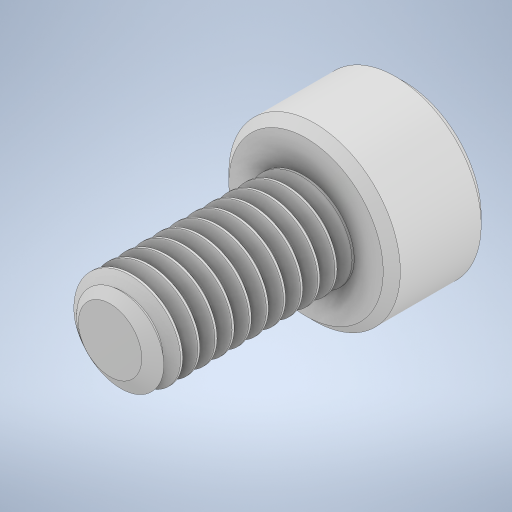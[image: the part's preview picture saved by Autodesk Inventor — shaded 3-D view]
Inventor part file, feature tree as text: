
AUTODESK INVENTOR PART (.ipt)
format: ipt  version: 2023 (Build 270158000, 158)  size: 627,200 bytes
history: native  units: in
note: dims shown in document units (in); Inventor stores cm internally (conversion verified against a paired STEP export)
features: other x2, chamfer x1
ambient origin geometry x8: Origin, YZ Plane, XZ Plane, XY Plane, X Axis, Y Axis, Z Axis, Center Point
bodies: Solid1 (feature_tree)
feature tree (3):
  other  "Table"
  other  "M4 8mm Bolt-01"
  chamfer  "Chamfer1"  [1 undecoded]
note: 1 required parameter value undecoded (feature->parameter linkage not recoverable at this tier; creation-order binding heuristic only, values carry confidence <= 0.55)
